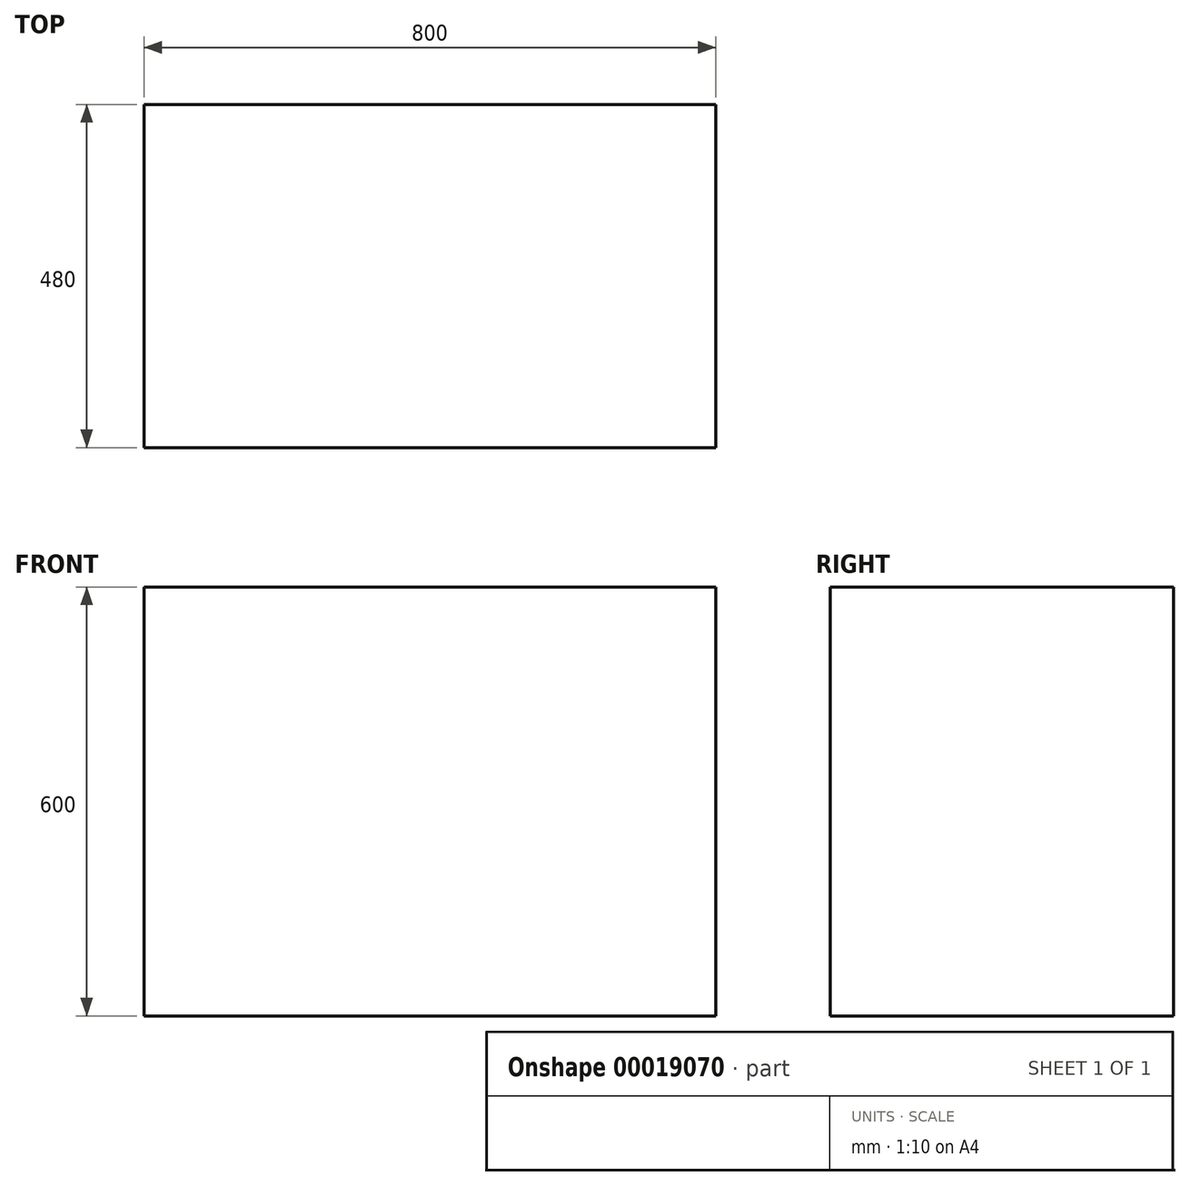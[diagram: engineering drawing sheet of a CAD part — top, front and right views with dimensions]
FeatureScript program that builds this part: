
annotation { "Feature Type Name" : "Feature", "Feature Type Description" : "" }
export const myFeature = defineFeature(function(context is Context, id is Id, definition is map)
    precondition{}
    {
        {
            var Q0;
            Q0=qCreatedBy(makeId("Top.planeOp"),FACE);
            var sketch = newSketch(context, id + "F0", { "sketchPlane" : qUnion([Q0])});
            skLineSegment(sketch, "E0.bottom", {"start": v(0, 0) * mm, "end": v(800, 0) * mm});
            skLineSegment(sketch, "E0.top", {"start": v(0, 480) * mm, "end": v(800, 480) * mm});
            skLineSegment(sketch, "E0.left", {"start": v(0, 0) * mm, "end": v(0, 480) * mm});
            skLineSegment(sketch, "E0.right", {"start": v(800, 0) * mm, "end": v(800, 480) * mm});
            skSolve(sketch);
        }
        {
            var Q0;
            Q0=makeQuery(id+"F0.imprint","IMPRINT",FACE,{"disambiguationData":[TD([[makeQuery(id+"F0.imprint","IMPRINT",EDGE,{"derivedFrom":sQuery(id+"F0.wireOp",EDGE,"E0.bottom")}),1.0]])]});
            extrude(context, id + "F1", {"entities" : qUnion([Q0]), "depth" : 600 * mm});
        }
    });
